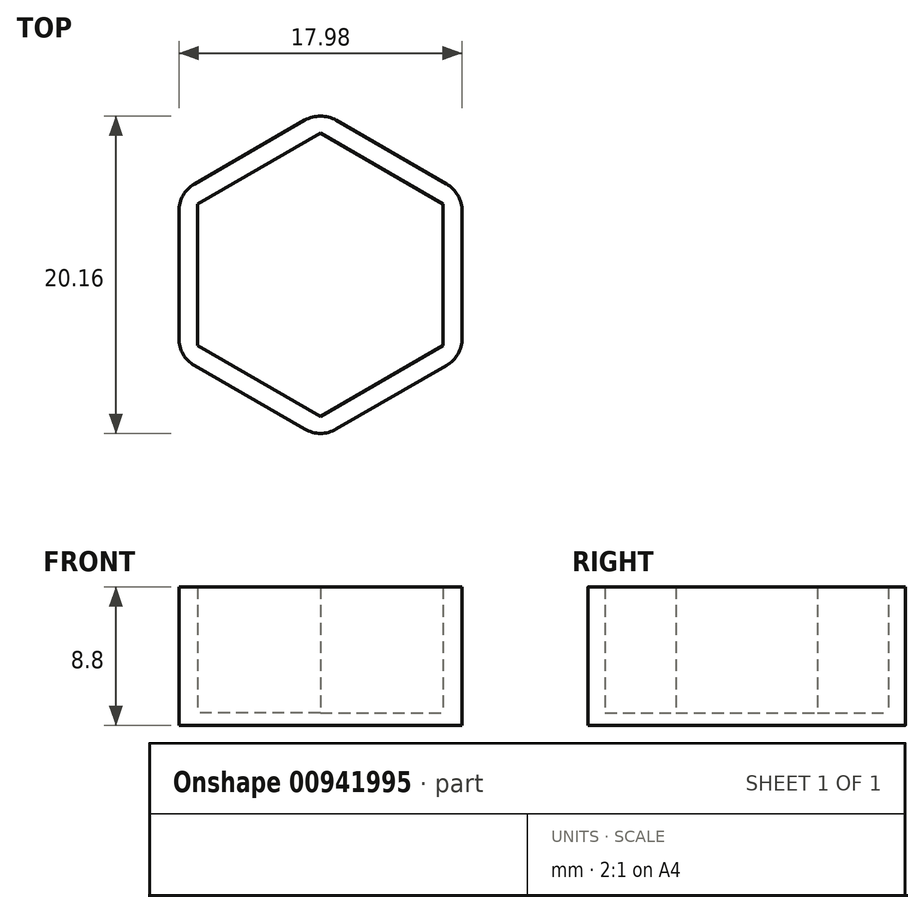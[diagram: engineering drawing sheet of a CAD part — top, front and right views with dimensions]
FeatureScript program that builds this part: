
annotation { "Feature Type Name" : "Feature", "Feature Type Description" : "" }
export const myFeature = defineFeature(function(context is Context, id is Id, definition is map)
    precondition{}
    {
        {
            var Q0;
            Q0=qCreatedBy(makeId("Top.planeOp"),FACE);
            var sketch = newSketch(context, id + "F0", { "sketchPlane" : qUnion([Q0])});
            skCircle(sketch, "E0.cCircle", {"center": v(0, 0) * mm, "radius": 7.8 * mm, "construction": true});
            skLineSegment(sketch, "E0.0", {"start": v(-7.8, -4.5) * mm, "end": v(-7.8, 4.5) * mm});
            skLineSegment(sketch, "E0.1", {"start": v(-7.8, 4.5) * mm, "end": v(0, 9) * mm});
            skLineSegment(sketch, "E0.2", {"start": v(0, 9) * mm, "end": v(7.8, 4.5) * mm});
            skLineSegment(sketch, "E0.3", {"start": v(7.8, 4.5) * mm, "end": v(7.8, -4.5) * mm});
            skLineSegment(sketch, "E0.4", {"start": v(7.8, -4.5) * mm, "end": v(0, -9) * mm});
            skLineSegment(sketch, "E0.5", {"start": v(0, -9) * mm, "end": v(-7.8, -4.5) * mm});
            skPoint(sketch, "E0.0.midPoint", {"position": v(-7.8, 0) * mm});
            skCircle(sketch, "E1.cCircle", {"center": v(0, 0) * mm, "radius": 9 * mm, "construction": true});
            skLineSegment(sketch, "E1.0", {"start": v(-9, -5.2) * mm, "end": v(-9, 5.2) * mm});
            skLineSegment(sketch, "E1.1", {"start": v(-9, 5.2) * mm, "end": v(0, 10.39) * mm});
            skLineSegment(sketch, "E1.2", {"start": v(0, 10.39) * mm, "end": v(9, 5.2) * mm});
            skLineSegment(sketch, "E1.3", {"start": v(9, 5.2) * mm, "end": v(9, -5.2) * mm});
            skLineSegment(sketch, "E1.4", {"start": v(9, -5.2) * mm, "end": v(0, -10.39) * mm});
            skLineSegment(sketch, "E1.5", {"start": v(0, -10.39) * mm, "end": v(-9, -5.2) * mm});
            skPoint(sketch, "E1.0.midPoint", {"position": v(-9, 0) * mm});
            skSolve(sketch);
        }
        {
            var Q0;
            Q0 = qSketchRegion(id + "F0", true);
            extrude(context, id + "F1", {"entities" : qUnion([Q0]), "depth" : 8 * mm, "offsetDistance" : 25 * mm});
        }
        {
            var Q0;
            Q0=makeQuery(id+"F0.imprint","IMPRINT",FACE,{"disambiguationData":[TD([[makeQuery(id+"F0.imprint","IMPRINT",EDGE,{"derivedFrom":sQuery(id+"F0.wireOp",EDGE,"E0.0")}),-1.0]])]});
            var Q1;
            Q1=makeQuery(id+"F0.imprint","IMPRINT",FACE,{"disambiguationData":[TD([[makeQuery(id+"F0.imprint","IMPRINT",EDGE,{"derivedFrom":sQuery(id+"F0.wireOp",EDGE,"E0.0")}),1.0]])]});
            extrude(context, id + "F2", {"entities" : qUnion([Q0, Q1]), "operationType" : NewBodyOperationType.ADD, "oppositeDirection" : true, "depth" : 0.8 * mm, "offsetDistance" : 25 * mm});
        }
        {
            var Q0;
            {var subQ0=sQuery(id+"F0.wireOp",EDGE,"E1.5");var subQ1=sQuery(id+"F0.wireOp",EDGE,"E1.0");Q0=makeQuery(id+"F2.boolean.opBoolean","MERGE",EDGE,{"derivedFrom":[makeQuery(id+"F1.opExtrude","SWEPT_EDGE",EDGE,{"disambiguationData":[OSD([subQ1,subQ0])]}),makeQuery(id+"F2.opExtrude","SWEPT_EDGE",EDGE,{"disambiguationData":[OSD([subQ1,subQ0])]})]});}
            var Q1;
            {var subQ0=sQuery(id+"F0.wireOp",EDGE,"E1.1");var subQ1=sQuery(id+"F0.wireOp",EDGE,"E1.0");Q1=makeQuery(id+"F2.boolean.opBoolean","MERGE",EDGE,{"derivedFrom":[makeQuery(id+"F1.opExtrude","SWEPT_EDGE",EDGE,{"disambiguationData":[OSD([subQ1,subQ0])]}),makeQuery(id+"F2.opExtrude","SWEPT_EDGE",EDGE,{"disambiguationData":[OSD([subQ1,subQ0])]})]});}
            var Q2;
            {var subQ0=sQuery(id+"F0.wireOp",EDGE,"E1.5");var subQ1=sQuery(id+"F0.wireOp",EDGE,"E1.4");Q2=makeQuery(id+"F2.boolean.opBoolean","MERGE",EDGE,{"derivedFrom":[makeQuery(id+"F1.opExtrude","SWEPT_EDGE",EDGE,{"disambiguationData":[OSD([subQ1,subQ0])]}),makeQuery(id+"F2.opExtrude","SWEPT_EDGE",EDGE,{"disambiguationData":[OSD([subQ1,subQ0])]})]});}
            var Q3;
            {var subQ0=sQuery(id+"F0.wireOp",EDGE,"E1.4");var subQ1=sQuery(id+"F0.wireOp",EDGE,"E1.3");Q3=makeQuery(id+"F2.boolean.opBoolean","MERGE",EDGE,{"derivedFrom":[makeQuery(id+"F1.opExtrude","SWEPT_EDGE",EDGE,{"disambiguationData":[OSD([subQ1,subQ0])]}),makeQuery(id+"F2.opExtrude","SWEPT_EDGE",EDGE,{"disambiguationData":[OSD([subQ1,subQ0])]})]});}
            var Q4;
            {var subQ0=sQuery(id+"F0.wireOp",EDGE,"E1.3");var subQ1=sQuery(id+"F0.wireOp",EDGE,"E1.2");Q4=makeQuery(id+"F2.boolean.opBoolean","MERGE",EDGE,{"derivedFrom":[makeQuery(id+"F1.opExtrude","SWEPT_EDGE",EDGE,{"disambiguationData":[OSD([subQ1,subQ0])]}),makeQuery(id+"F2.opExtrude","SWEPT_EDGE",EDGE,{"disambiguationData":[OSD([subQ1,subQ0])]})]});}
            var Q5;
            {var subQ0=sQuery(id+"F0.wireOp",EDGE,"E1.2");var subQ1=sQuery(id+"F0.wireOp",EDGE,"E1.1");Q5=makeQuery(id+"F2.boolean.opBoolean","MERGE",EDGE,{"derivedFrom":[makeQuery(id+"F1.opExtrude","SWEPT_EDGE",EDGE,{"disambiguationData":[OSD([subQ1,subQ0])]}),makeQuery(id+"F2.opExtrude","SWEPT_EDGE",EDGE,{"disambiguationData":[OSD([subQ1,subQ0])]})]});}
            fillet(context, id + "F3", {"entities" : qUnion([Q0, Q1, Q2, Q3, Q4, Q5]), "radius" : 2 * mm, "tangentPropagation" : true, "allowEdgeOverflow" : false});
        }
    });
